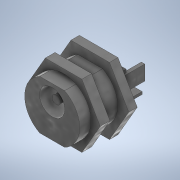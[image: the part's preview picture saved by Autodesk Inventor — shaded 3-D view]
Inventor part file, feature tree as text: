
AUTODESK INVENTOR PART (.ipt)
format: ipt  version: 2020.5 (Build 245400000, 400)  size: 180,736 bytes
history: native  units: mm
features: extrude x8, sketch x1
ambient origin geometry x8: Origin, YZ Plane, XZ Plane, XY Plane, X Axis, Y Axis, Z Axis, Center Point
bodies: Body1 (feature_tree)
feature tree (9):
  sketch  "Sketch1"  dims[d28=9.0mm d29=0.0mm d30=2.0mm d31=0.0mm d32=2.0mm d33=0.0mm d34=4.9mm d35=0.0mm d36=6.0mm d37=0.0mm d38=6.3mm d39=0.0mm d40=4.0mm d41=0.0mm d42=8.0mm d43=0.0mm d25=0.5mm d26=0.872665mm d27=0.5mm]
  extrude  "Extrusion4"  Depth=2.0mm TaperAngle=0.0deg
  extrude  "Extrusion5"  Depth=2.0mm TaperAngle=0.0deg
  extrude  "Extrusion6"  Depth=4.9mm TaperAngle=0.0deg
  extrude  "Extrusion7"  Depth=6.0mm TaperAngle=0.0deg
  extrude  "Extrusion8"  Depth=6.3mm TaperAngle=0.0deg
  extrude  "Extrusion9"  Depth=4.0mm TaperAngle=0.0deg
  extrude  "Extrusion10"  Depth=8.0mm TaperAngle=0.0deg
  extrude  "Extrusion11"  Depth=8.0mm
